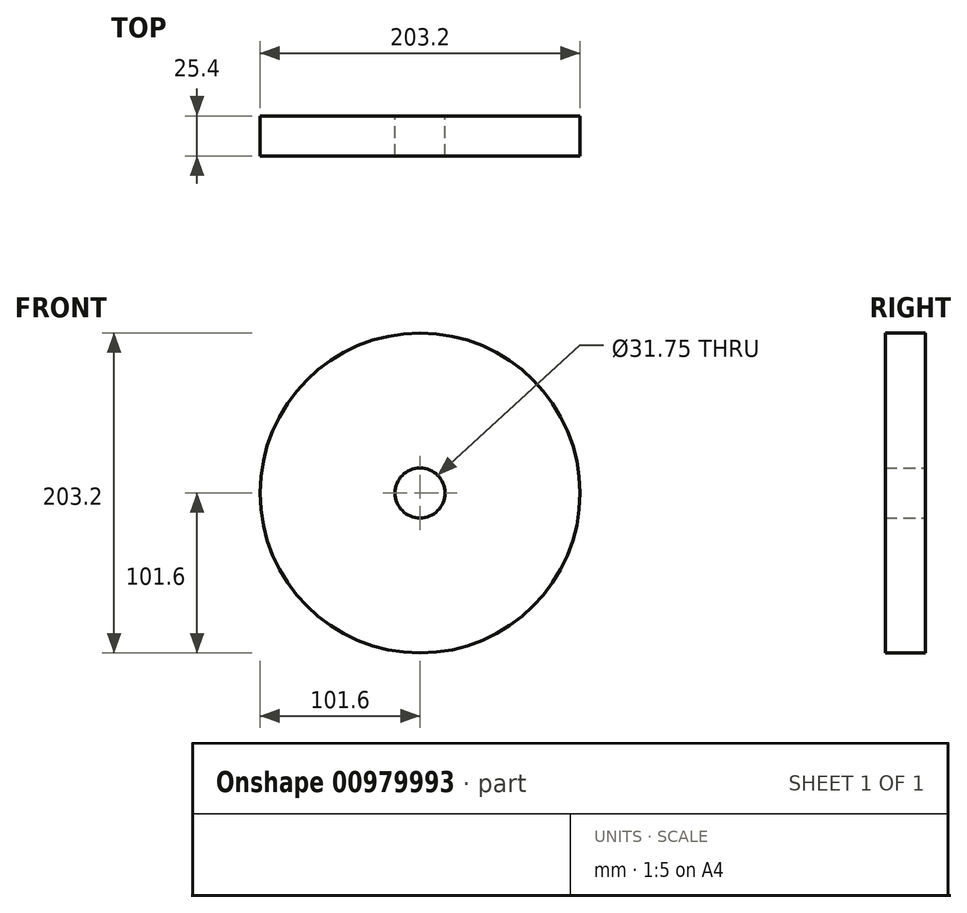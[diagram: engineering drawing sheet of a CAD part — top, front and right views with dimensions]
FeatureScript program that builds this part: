
annotation { "Feature Type Name" : "Feature", "Feature Type Description" : "" }
export const myFeature = defineFeature(function(context is Context, id is Id, definition is map)
    precondition{}
    {
        {
            var Q0;
            Q0=qCreatedBy(makeId("Front.planeOp"),FACE);
            var sketch = newSketch(context, id + "F0", { "sketchPlane" : qUnion([Q0])});
            skCircle(sketch, "E0", {"center": v(0, 0) * mm, "radius": 101.6 * mm});
            skSolve(sketch);
        }
        {
            var Q0;
            Q0=makeQuery(id+"F0.imprint","IMPRINT",FACE,{"disambiguationData":[TD([[makeQuery(id+"F0.imprint","IMPRINT",EDGE,{"derivedFrom":sQuery(id+"F0.wireOp",EDGE,"E0")}),1.0]])]});
            var sketch = newSketch(context, id + "F1", { "sketchPlane" : qUnion([Q0])});
            skCircle(sketch, "E1", {"center": v(0, 0) * mm, "radius": 15.88 * mm});
            skSolve(sketch);
        }
        {
            var Q0;
            Q0=makeQuery(id+"F1.imprint","IMPRINT",FACE,{"disambiguationData":[TD([[makeQuery(id+"F1.imprint","IMPRINT",EDGE,{"derivedFrom":sQuery(id+"F1.wireOp",EDGE,"E1")}),-1.0]])]});
            extrude(context, id + "F2", {"entities" : qUnion([Q0]), "depth" : 25.4 * mm, "offsetDistance" : 25.4 * mm});
        }
    });
